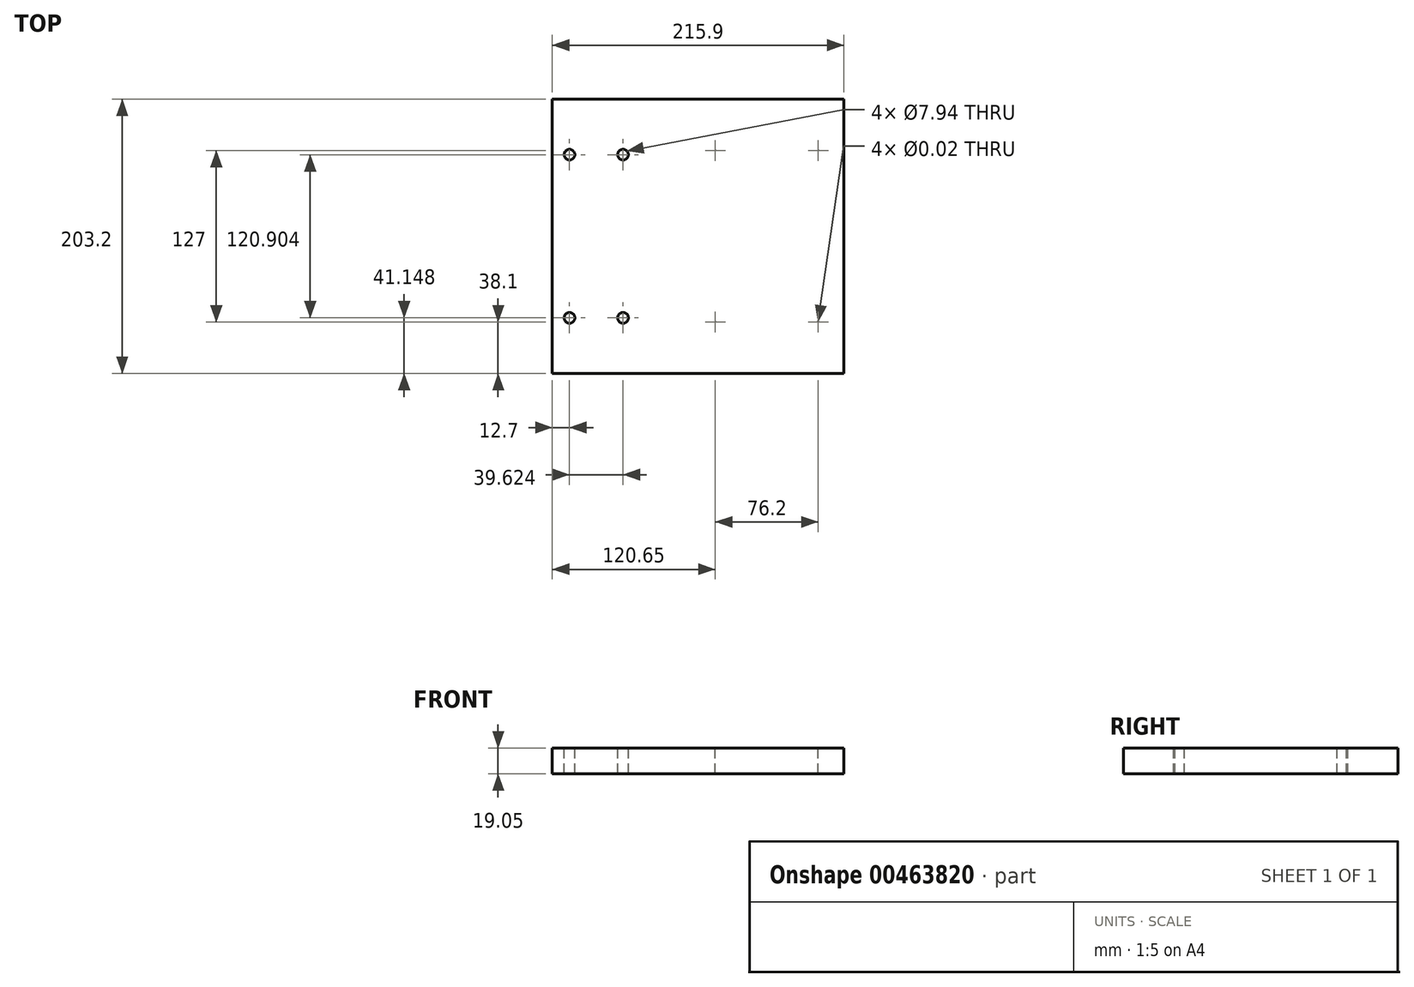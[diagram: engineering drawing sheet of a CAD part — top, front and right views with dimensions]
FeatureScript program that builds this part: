
annotation { "Feature Type Name" : "Feature", "Feature Type Description" : "" }
export const myFeature = defineFeature(function(context is Context, id is Id, definition is map)
    precondition{}
    {
        {
            var Q0;
            Q0=qCreatedBy(makeId("Top.planeOp"),FACE);
            var sketch = newSketch(context, id + "F0", { "sketchPlane" : qUnion([Q0])});
            skLineSegment(sketch, "E0.bottom", {"start": v(-107.95, 101.6) * mm, "end": v(107.95, 101.6) * mm});
            skLineSegment(sketch, "E0.top", {"start": v(-107.95, -101.6) * mm, "end": v(107.95, -101.6) * mm});
            skLineSegment(sketch, "E0.left", {"start": v(-107.95, 101.6) * mm, "end": v(-107.95, -101.6) * mm});
            skLineSegment(sketch, "E0.right", {"start": v(107.95, 101.6) * mm, "end": v(107.95, -101.6) * mm});
            skPoint(sketch, "E0.middle", {"position": v(0, 0) * mm});
            skSolve(sketch);
        }
        {
            var Q0;
            Q0 = qSketchRegion(id + "F0", true);
            extrude(context, id + "F1", {"entities" : qUnion([Q0]), "depth" : 19.05 * mm});
        }
        {
            var Q0;
            Q0=makeQuery(id+"F1.opExtrude","CAP_FACE",FACE,{"disambiguationData":[OSD([sQuery(id+"F0.wireOp",EDGE,"E0.bottom"),sQuery(id+"F0.wireOp",EDGE,"E0.top"),sQuery(id+"F0.wireOp",EDGE,"E0.left"),sQuery(id+"F0.wireOp",EDGE,"E0.right")])],"isStart":false});
            var sketch = newSketch(context, id + "F2", { "sketchPlane" : qUnion([Q0])});
            skLineSegment(sketch, "E1", {"start": v(-154.4, 0) * mm, "end": v(133.87, 0) * mm, "construction": true});
            skLineSegment(sketch, "E2.0", {"start": v(107.95, 101.6) * mm, "end": v(107.95, -101.6) * mm, "construction": true});
            skLineSegment(sketch, "E3.0", {"start": v(88.9, 101.6) * mm, "end": v(88.9, -101.6) * mm, "construction": true});
            skLineSegment(sketch, "E4.0", {"start": v(12.7, 101.6) * mm, "end": v(12.7, -101.6) * mm, "construction": true});
            skLineSegment(sketch, "E5.0", {"start": v(-154.4, -63.5) * mm, "end": v(133.87, -63.5) * mm, "construction": true});
            skPoint(sketch, "E6", {"position": v(12.7, -63.5) * mm});
            skPoint(sketch, "E7", {"position": v(88.9, -63.5) * mm});
            skPoint(sketch, "E8.MirrorP", {"position": v(12.7, 63.5) * mm});
            skPoint(sketch, "E9.MirrorP", {"position": v(88.9, 63.5) * mm});
            skLineSegment(sketch, "E10.0", {"start": v(-107.95, 101.6) * mm, "end": v(-107.95, -101.6) * mm, "construction": true});
            skLineSegment(sketch, "E11.0", {"start": v(-95.25, 101.6) * mm, "end": v(-95.25, -101.6) * mm, "construction": true});
            skLineSegment(sketch, "E12.0", {"start": v(-55.63, 101.6) * mm, "end": v(-55.63, -101.6) * mm, "construction": true});
            skLineSegment(sketch, "E13.0", {"start": v(-154.4, 60.45) * mm, "end": v(133.87, 60.45) * mm, "construction": true});
            skPoint(sketch, "E14", {"position": v(-95.25, 60.45) * mm});
            skPoint(sketch, "E15", {"position": v(-55.63, 60.45) * mm});
            skPoint(sketch, "E16.MirrorP", {"position": v(-95.25, -60.45) * mm});
            skPoint(sketch, "E17.MirrorP", {"position": v(-55.63, -60.45) * mm});
            skSolve(sketch);
        }
        {
            var Q0;
            Q0=sQuery(id+"F2.wireOp",VERTEX,"E14");
            var Q1;
            Q1=sQuery(id+"F2.wireOp",VERTEX,"E15");
            var Q2;
            Q2=sQuery(id+"F2.wireOp",VERTEX,"E16.MirrorP");
            var Q3;
            Q3=sQuery(id+"F2.wireOp",VERTEX,"E17.MirrorP");
            var Q4;
            Q4=makeQuery(id+"F1.opExtrude","SWEPT_BODY",BODY,{"disambiguationData":[OSD([sQuery(id+"F0.wireOp",EDGE,"E0.bottom"),sQuery(id+"F0.wireOp",EDGE,"E0.top"),sQuery(id+"F0.wireOp",EDGE,"E0.left"),sQuery(id+"F0.wireOp",EDGE,"E0.right")])]});
            hole(context, id + "F3", {"style" : HoleStyle.SIMPLE, "endStyle" : HoleEndStyle.THROUGH, "standardTappedOrClearance" : lookupTablePath({ "standard" : "ANSI", "engagement" : "75%", "pitch" : "16 tpi", "size" : "3/8", "type" : "Tapped" }), "standardBlindInLast" : lookupTablePath({ "standard" : "ANSI", "engagement" : "75%", "pitch" : "16 tpi", "size" : "3/8", "type" : "Tapped" }), "holeDiameter" : 7.94 * mm, "showTappedDepth" : true, "isTappedThrough" : true, "tappedDepth" : 22.22 * mm, "tapClearance" : 3, "locations" : qUnion([Q0, Q1, Q2, Q3]), "scope" : qUnion([Q4]), "majorDiameter" : 9.53 * mm});
        }
        {
            var Q0;
            Q0=sQuery(id+"F2.wireOp",VERTEX,"E8.MirrorP");
            var Q1;
            Q1=sQuery(id+"F2.wireOp",VERTEX,"E9.MirrorP");
            var Q2;
            Q2=sQuery(id+"F2.wireOp",VERTEX,"E6");
            var Q3;
            Q3=sQuery(id+"F2.wireOp",VERTEX,"E7");
            var Q4;
            Q4=makeQuery(id+"F1.opExtrude","SWEPT_BODY",BODY,{"disambiguationData":[OSD([sQuery(id+"F0.wireOp",EDGE,"E0.bottom"),sQuery(id+"F0.wireOp",EDGE,"E0.top"),sQuery(id+"F0.wireOp",EDGE,"E0.left"),sQuery(id+"F0.wireOp",EDGE,"E0.right")])]});
            hole(context, id + "F4", {"style" : HoleStyle.SIMPLE, "endStyle" : HoleEndStyle.THROUGH, "standardTappedOrClearance" : lookupTablePath({ "standard" : "ANSI", "size" : "7/16 (0.44)", "type" : "Drilled" }), "standardBlindInLast" : lookupTablePath({ "standard" : "ANSI", "size" : "7/16", "type" : "Drilled" }), "holeDiameter" : 7 / 406.4 * mm, "isTappedThrough" : true, "tappedDepth" : 22.22 * mm, "tapClearance" : 3, "locations" : qUnion([Q0, Q1, Q2, Q3]), "scope" : qUnion([Q4])});
        }
    });
